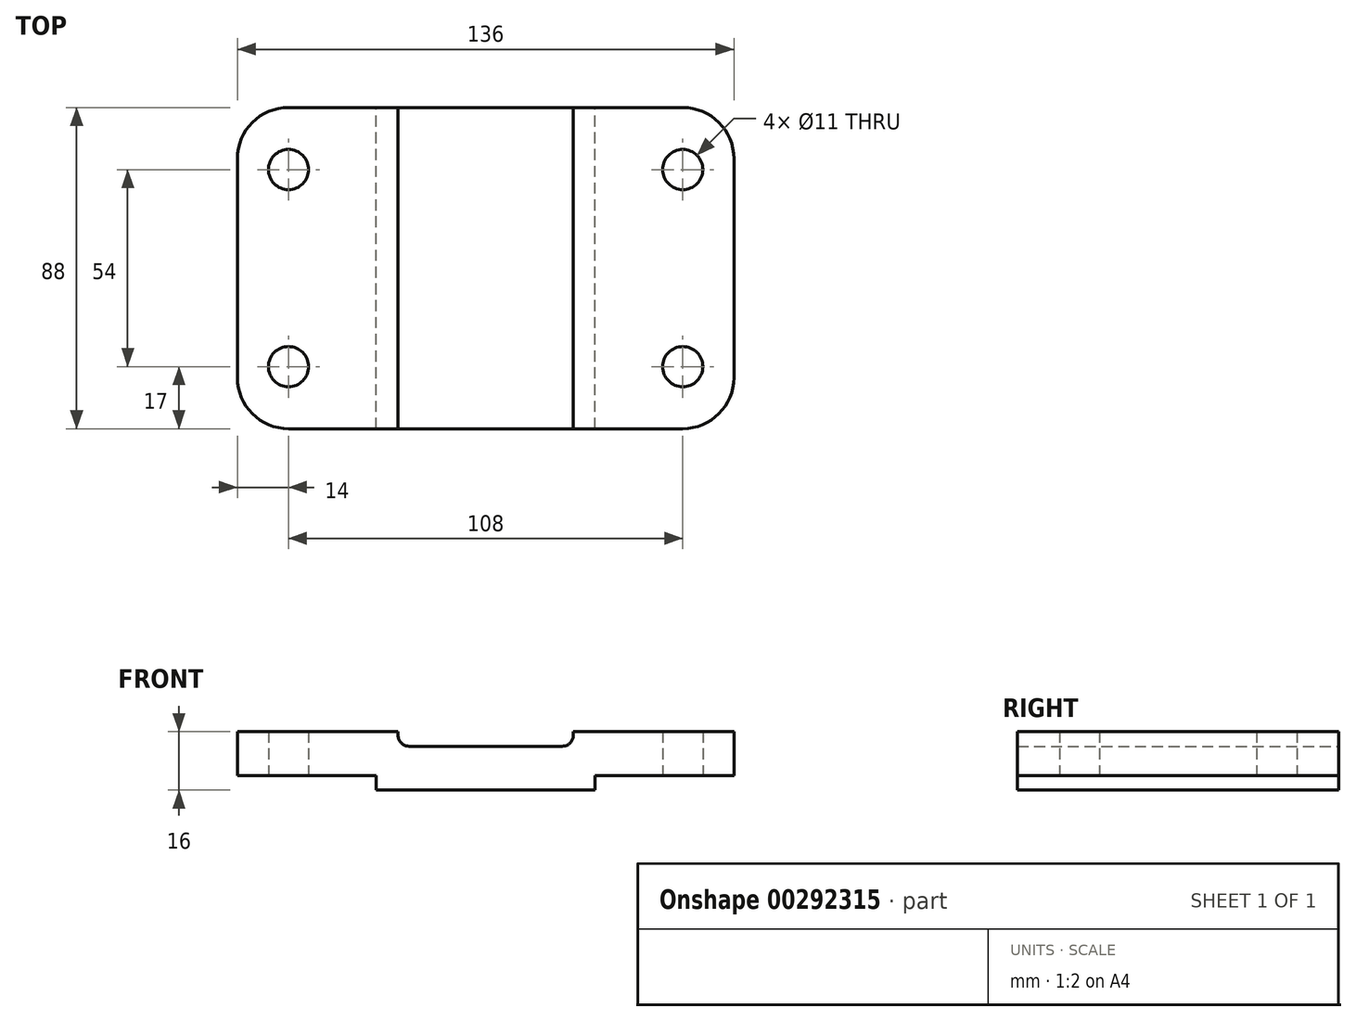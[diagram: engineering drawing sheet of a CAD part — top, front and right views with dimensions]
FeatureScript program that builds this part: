
annotation { "Feature Type Name" : "Feature", "Feature Type Description" : "" }
export const myFeature = defineFeature(function(context is Context, id is Id, definition is map)
    precondition{}
    {
        {
            var Q0;
            Q0=qCreatedBy(makeId("Front.planeOp"),FACE);
            var sketch = newSketch(context, id + "F0", { "sketchPlane" : qUnion([Q0])});
            skLineSegment(sketch, "E0.bottom", {"start": v(-30, 0) * mm, "end": v(30, 0) * mm});
            skLineSegment(sketch, "E0.top", {"start": v(-21, 12) * mm, "end": v(21, 12) * mm});
            skLineSegment(sketch, "E0.left", {"start": v(-30, 0) * mm, "end": v(-30, 4) * mm});
            skLineSegment(sketch, "E0.right", {"start": v(30, 0) * mm, "end": v(30, 4) * mm});
            skLineSegment(sketch, "E1.bottom", {"start": v(30, 4) * mm, "end": v(68, 4) * mm});
            skLineSegment(sketch, "E1.top", {"start": v(24, 16) * mm, "end": v(68, 16) * mm});
            skLineSegment(sketch, "E1.left", {"start": v(24, 15) * mm, "end": v(24, 16) * mm});
            skLineSegment(sketch, "E1.right", {"start": v(68, 4) * mm, "end": v(68, 16) * mm});
            skLineSegment(sketch, "E2.MirrorCS", {"start": v(-24, 16) * mm, "end": v(-68, 16) * mm});
            skLineSegment(sketch, "E3.MirrorCS", {"start": v(-30, 4) * mm, "end": v(-68, 4) * mm});
            skLineSegment(sketch, "E4.MirrorCS", {"start": v(-24, 15) * mm, "end": v(-24, 16) * mm});
            skLineSegment(sketch, "E5.MirrorCS", {"start": v(-68, 4) * mm, "end": v(-68, 16) * mm});
            skPoint(sketch, "E6.visualSharp", {"position": v(-24, 12) * mm});
            skArc(sketch, "E6.filletArc", {"start": v(-24, 15) * mm, "mid": v(-23.12, 12.88) * mm, "end": v(-21, 12) * mm});
            skPoint(sketch, "E7.visualSharp", {"position": v(24, 12) * mm});
            skArc(sketch, "E7.filletArc", {"start": v(21, 12) * mm, "mid": v(23.12, 12.88) * mm, "end": v(24, 15) * mm});
            skSolve(sketch);
        }
        {
            var Q0;
            Q0 = qSketchRegion(id + "F0", true);
            extrude(context, id + "F1", {"entities" : qUnion([Q0]), "endBound" : BoundingType.SYMMETRIC, "depth" : 88 * mm});
        }
        {
            var Q0;
            Q0=makeQuery(id+"F1.opExtrude","CAP_EDGE",EDGE,{"disambiguationData":[OSD([sQuery(id+"F0.wireOp",EDGE,"E5.MirrorCS")])],"isStart":false});
            var Q1;
            Q1=makeQuery(id+"F1.opExtrude","CAP_EDGE",EDGE,{"disambiguationData":[OSD([sQuery(id+"F0.wireOp",EDGE,"E5.MirrorCS")])],"isStart":true});
            var Q2;
            Q2=makeQuery(id+"F1.opExtrude","CAP_EDGE",EDGE,{"disambiguationData":[OSD([sQuery(id+"F0.wireOp",EDGE,"E1.right")])],"isStart":true});
            var Q3;
            Q3=makeQuery(id+"F1.opExtrude","CAP_EDGE",EDGE,{"disambiguationData":[OSD([sQuery(id+"F0.wireOp",EDGE,"E1.right")])],"isStart":false});
            fillet(context, id + "F2", {"entities" : qUnion([Q0, Q1, Q2, Q3]), "radius" : 14 * mm, "tangentPropagation" : true, "allowEdgeOverflow" : false});
        }
        {
            var Q0;
            Q0=qCreatedBy(makeId("Top.planeOp"),FACE);
            var sketch = newSketch(context, id + "F3", { "sketchPlane" : qUnion([Q0])});
            skCircle(sketch, "E8", {"center": v(-54, 27) * mm, "radius": 5.5 * mm});
            skCircle(sketch, "E9.0.1.0", {"center": v(-54, -27) * mm, "radius": 5.5 * mm});
            skCircle(sketch, "E9.1.0.0", {"center": v(54, 27) * mm, "radius": 5.5 * mm});
            skCircle(sketch, "E9.1.1.0", {"center": v(54, -27) * mm, "radius": 5.5 * mm});
            skLineSegment(sketch, "E9.direction1", {"start": v(-54, 27) * mm, "end": v(54, 27) * mm, "construction": true});
            skLineSegment(sketch, "E9.direction2", {"start": v(-54, 27) * mm, "end": v(-54, -27) * mm, "construction": true});
            skPoint(sketch, "E10", {"position": v(0, 27) * mm});
            skPoint(sketch, "E11", {"position": v(-54, 0) * mm});
            skSolve(sketch);
        }
        {
            var Q0;
            Q0 = qSketchRegion(id + "F3", true);
            extrude(context, id + "F4", {"entities" : qUnion([Q0]), "operationType" : NewBodyOperationType.REMOVE, "endBound" : BoundingType.THROUGH_ALL, "depth" : 25 * mm});
        }
    });
